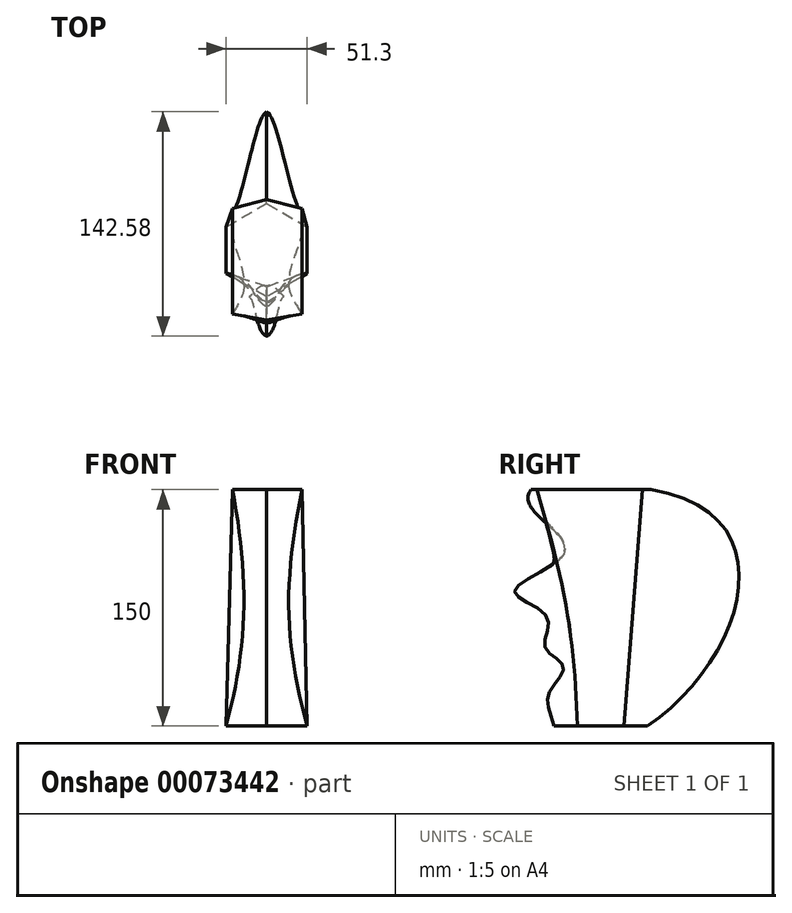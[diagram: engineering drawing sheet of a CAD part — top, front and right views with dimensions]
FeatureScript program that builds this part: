
annotation { "Feature Type Name" : "Feature", "Feature Type Description" : "" }
export const myFeature = defineFeature(function(context is Context, id is Id, definition is map)
    precondition{}
    {
        {
            var Q0;
            Q0=qCreatedBy(makeId("Top.planeOp"),FACE);
            cPlane(context, id + "F0", {"entities" : qUnion([Q0]), "cplaneType" : CPlaneType.OFFSET, "offset" : 150 * mm, "width" : 150 * mm, "height" : 150 * mm});
        }
        {
            var Q0;
            Q0=qCreatedBy(makeId("Top.planeOp"),FACE);
            var sketch = newSketch(context, id + "F1", { "sketchPlane" : qUnion([Q0])});
            skCircle(sketch, "E0.cCircle", {"center": v(0, 0) * mm, "radius": 29.62 * mm, "construction": true});
            skLineSegment(sketch, "E0.0", {"start": v(0, -29.62) * mm, "end": v(-25.65, -14.8) * mm});
            skLineSegment(sketch, "E0.1", {"start": v(-25.65, -14.8) * mm, "end": v(-25.65, 14.8) * mm});
            skLineSegment(sketch, "E0.2", {"start": v(-25.65, 14.8) * mm, "end": v(0, 29.62) * mm});
            skLineSegment(sketch, "E0.3", {"start": v(0, 29.62) * mm, "end": v(25.65, 14.8) * mm});
            skLineSegment(sketch, "E0.4", {"start": v(25.65, 14.8) * mm, "end": v(25.65, -14.8) * mm});
            skLineSegment(sketch, "E0.5", {"start": v(25.65, -14.8) * mm, "end": v(0, -29.62) * mm});
            skSolve(sketch);
        }
        {
            var Q0;
            Q0=qCreatedBy(id+"F0.planeOp",FACE);
            var sketch = newSketch(context, id + "F2", { "sketchPlane" : qUnion([Q0])});
            skLineSegment(sketch, "E1.left", {"start": v(-21.76, -40.46) * mm, "end": v(-21.76, 26.33) * mm});
            skLineSegment(sketch, "E1.right", {"start": v(22.35, -40.46) * mm, "end": v(22.35, 26.33) * mm});
            skLineSegment(sketch, "E2", {"start": v(0, 32) * mm, "end": v(-21.76, 26.33) * mm});
            skLineSegment(sketch, "E3", {"start": v(-21.76, -40.46) * mm, "end": v(0, -44.47) * mm});
            skLineSegment(sketch, "E4", {"start": v(22.35, -40.46) * mm, "end": v(0, -44.47) * mm});
            skLineSegment(sketch, "E5", {"start": v(22.35, 26.33) * mm, "end": v(0, 32) * mm});
            skSolve(sketch);
        }
        {
            var Q0;
            Q0=qCreatedBy(makeId("Right.planeOp"),FACE);
            var sketch = newSketch(context, id + "F3", { "sketchPlane" : qUnion([Q0])});
            skFitSpline(sketch, "E6", {"points": [v(29.62, 0) * mm, v(32, 150) * mm], "startDerivative": vector(178.59, 119.19) * mm, "endDerivative": vector(-271.92, 44.97) * mm});
            skFitSpline(sketch, "E7", {"points": [v(-29.62, 0) * mm, v(-32.86, 20.72) * mm, v(-23.7, 37.83) * mm, v(-35.5, 50.12) * mm, v(-34, 69.14) * mm, v(-54.67, 85.33) * mm, v(-24.35, 107.95) * mm, v(-33.1, 127.23) * mm, v(-44.47, 150) * mm], "startDerivative": vector(-56.34, 224.35) * mm, "endDerivative": vector(134.32, 182.65) * mm});
            skSolve(sketch);
        }
        {
            var Q0;
            Q0=sQuery(id+"F1.wireOp",VERTEX,"E0.5.start");
            var Q1;
            Q1=sQuery(id+"F1.wireOp",VERTEX,"E0.2.start");
            var Q2;
            Q2=sQuery(id+"F2.wireOp",VERTEX,"E1.right.start");
            cPlane(context, id + "F4", {"entities" : qUnion([Q0, Q1, Q2]), "cplaneType" : CPlaneType.THREE_POINT, "offset" : 150 * mm, "width" : 150 * mm, "height" : 150 * mm});
        }
        {
            var Q0;
            Q0=qCreatedBy(id+"F4.planeOp",FACE);
            var sketch = newSketch(context, id + "F5", { "sketchPlane" : qUnion([Q0])});
            skFitSpline(sketch, "E8", {"points": [v(29.5, 2.68) * mm, v(16.15, 73.87) * mm, v(25.7, 154.84) * mm], "startDerivative": vector(-43.74, 143.34) * mm, "endDerivative": vector(34.17, 159.84) * mm});
            skSolve(sketch);
        }
        {
            var Q0;
            Q0=sQuery(id+"F1.wireOp",VERTEX,"E0.1.start");
            var Q1;
            Q1=sQuery(id+"F1.wireOp",VERTEX,"E0.4.start");
            var Q2;
            Q2=sQuery(id+"F2.wireOp",VERTEX,"E3.start");
            cPlane(context, id + "F6", {"entities" : qUnion([Q0, Q1, Q2]), "cplaneType" : CPlaneType.THREE_POINT, "offset" : 150 * mm, "width" : 150 * mm, "height" : 150 * mm});
        }
        {
            var Q0;
            Q0=qCreatedBy(id+"F6.planeOp",FACE);
            var sketch = newSketch(context, id + "F7", { "sketchPlane" : qUnion([Q0])});
            skFitSpline(sketch, "E9", {"points": [v(29.5, 2.7) * mm, v(16.7, 73.7) * mm, v(25.02, 154.87) * mm], "startDerivative": vector(-43.74, 143.34) * mm, "endDerivative": vector(34.17, 159.84) * mm});
            skSolve(sketch);
        }
        {
            var Q0;
            Q0=makeQuery(id+"F1.imprint","IMPRINT",FACE,{"disambiguationData":[TD([[makeQuery(id+"F1.imprint","IMPRINT",EDGE,{"derivedFrom":sQuery(id+"F1.wireOp",EDGE,"E0.0")}),-1.0]])]});
            var Q1;
            Q1=makeQuery(id+"F2.imprint","IMPRINT",FACE,{"disambiguationData":[TD([[makeQuery(id+"F2.imprint","IMPRINT",EDGE,{"derivedFrom":sQuery(id+"F2.wireOp",EDGE,"E1.left")}),-1.0]])]});
            var Q2;
            Q2=sQuery(id+"F3.wireOp",EDGE,"E6");
            var Q3;
            Q3=sQuery(id+"F3.wireOp",EDGE,"E7");
            var Q4;
            Q4=sQuery(id+"F7.wireOp",EDGE,"E9");
            var Q5;
            Q5=sQuery(id+"F5.wireOp",EDGE,"E8");
            loft(context, id + "F8", {"addGuides" : true, "sheetProfilesArray" : [{ "sheetProfileEntities" : qUnion([Q0]) }, { "sheetProfileEntities" : qUnion([Q1]) }], "guidesArray" : [{ "guideEntities" : qUnion([Q2]), "guideDerivativeType" : LoftGuideDerivativeType.DEFAULT, "guideDerivativeMagnitude" : 1 }, { "guideEntities" : qUnion([Q3]), "guideDerivativeType" : LoftGuideDerivativeType.DEFAULT, "guideDerivativeMagnitude" : 1 }, { "guideEntities" : qUnion([Q4]), "guideDerivativeType" : LoftGuideDerivativeType.DEFAULT, "guideDerivativeMagnitude" : 1 }, { "guideEntities" : qUnion([Q5]), "guideDerivativeType" : LoftGuideDerivativeType.DEFAULT, "guideDerivativeMagnitude" : 1 }]});
        }
    });
